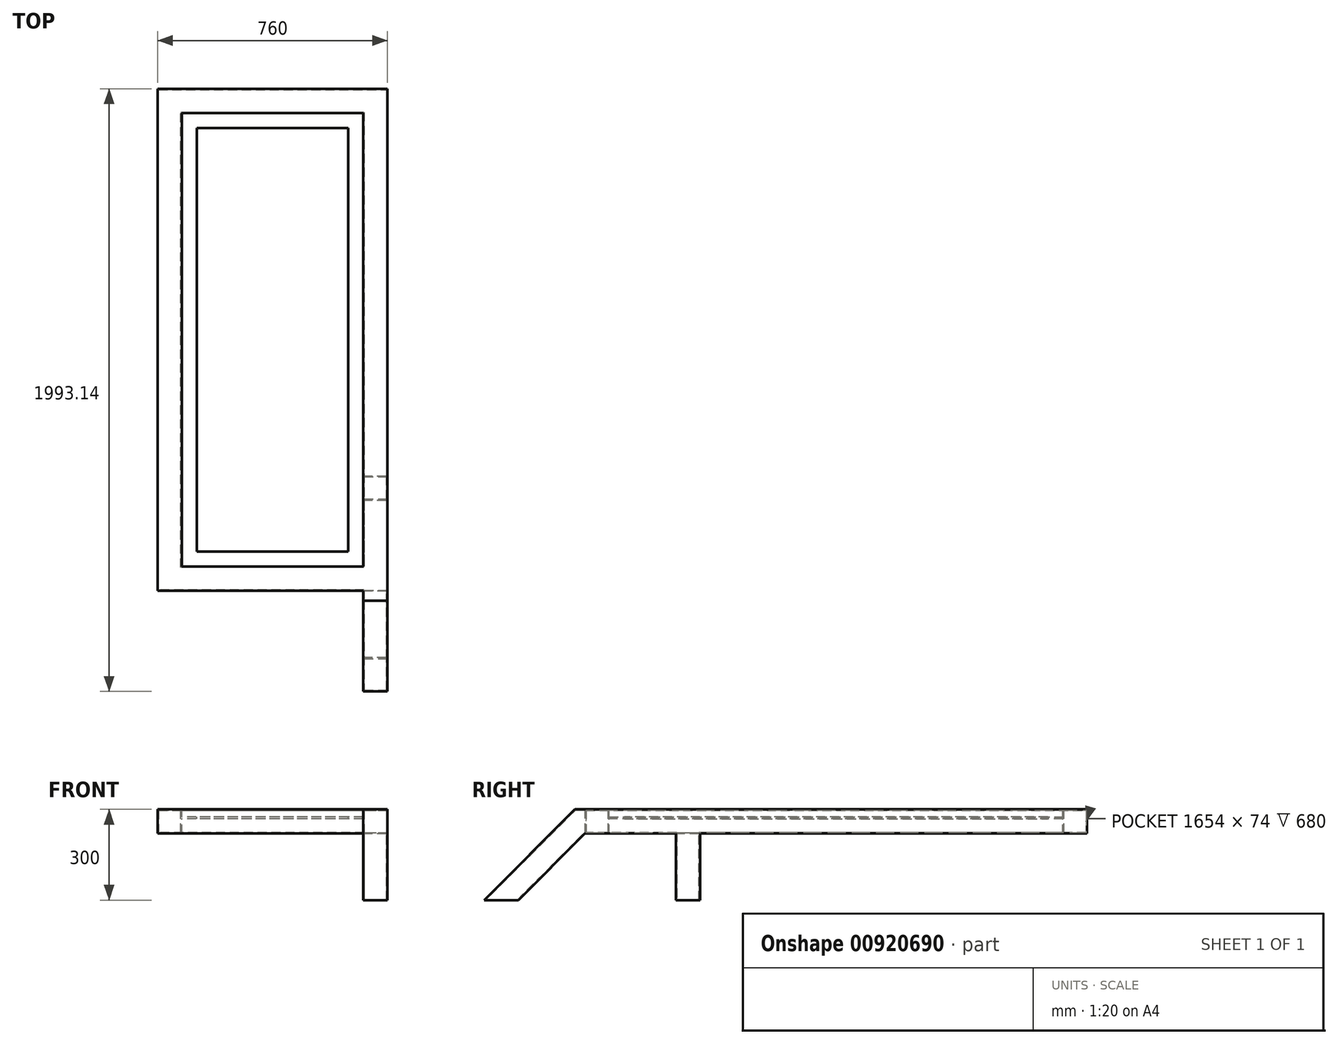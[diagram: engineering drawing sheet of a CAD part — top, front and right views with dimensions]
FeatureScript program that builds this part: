
annotation { "Feature Type Name" : "Feature", "Feature Type Description" : "" }
export const myFeature = defineFeature(function(context is Context, id is Id, definition is map)
    precondition{}
    {
        {
            var Q0;
            Q0=qCreatedBy(makeId("Top.planeOp"),FACE);
            var sketch = newSketch(context, id + "F0", { "sketchPlane" : qUnion([Q0])});
            skLineSegment(sketch, "E0.bottom", {"start": v(0, 0) * mm, "end": v(600, 0) * mm});
            skLineSegment(sketch, "E0.top", {"start": v(0, 1500) * mm, "end": v(600, 1500) * mm});
            skLineSegment(sketch, "E0.left", {"start": v(0, 0) * mm, "end": v(0, 1500) * mm});
            skLineSegment(sketch, "E0.right", {"start": v(600, 0) * mm, "end": v(600, 1500) * mm});
            skSolve(sketch);
        }
        {
            var Q0;
            Q0=qCreatedBy(makeId("Front.planeOp"),FACE);
            var sketch = newSketch(context, id + "F1", { "sketchPlane" : qUnion([Q0])});
            skLineSegment(sketch, "E1.bottom", {"start": v(0, -50) * mm, "end": v(-80, -50) * mm});
            skLineSegment(sketch, "E1.top", {"start": v(0, 30) * mm, "end": v(-80, 30) * mm});
            skLineSegment(sketch, "E1.left", {"start": v(0, -50) * mm, "end": v(0, -1) * mm});
            skLineSegment(sketch, "E1.right", {"start": v(-80, -50) * mm, "end": v(-80, 30) * mm});
            skLineSegment(sketch, "E2.bottom", {"start": v(0, 5) * mm, "end": v(50, 5) * mm});
            skLineSegment(sketch, "E2.top", {"start": v(0, -1) * mm, "end": v(50, -1) * mm});
            skLineSegment(sketch, "E2.right", {"start": v(50, 5) * mm, "end": v(50, -1) * mm});
            skLineSegment(sketch, "E3.trimOffspring", {"start": v(0, 5) * mm, "end": v(0, 30) * mm});
            skSolve(sketch);
        }
        {
            var Q0;
            Q0=makeQuery(id+"F1.imprint","IMPRINT",FACE,{"disambiguationData":[TD([[makeQuery(id+"F1.imprint","IMPRINT",EDGE,{"derivedFrom":sQuery(id+"F1.wireOp",EDGE,"E1.bottom")}),-1.0]])]});
            var Q1;
            Q1=sQuery(id+"F0.wireOp",EDGE,"E0.left");
            var Q2;
            Q2=sQuery(id+"F0.wireOp",EDGE,"E0.top");
            var Q3;
            Q3=sQuery(id+"F0.wireOp",EDGE,"E0.right");
            var Q4;
            Q4=sQuery(id+"F0.wireOp",EDGE,"E0.bottom");
            sweep(context, id + "F2", {"profiles" : qUnion([Q0]), "path" : qUnion([Q1, Q2, Q3, Q4])});
        }
        {
            var Q0;
            Q0=makeQuery(id+"F2.opSweep","SWEPT_FACE",FACE,{"disambiguationData":[OSD([sQuery(id+"F0.wireOp",EDGE,"E0.right"),sQuery(id+"F1.wireOp",EDGE,"E1.right")])]});
            var sketch = newSketch(context, id + "F3", { "sketchPlane" : qUnion([Q0])});
            skLineSegment(sketch, "E4", {"start": v(-80, 30) * mm, "end": v(-113.14, 30) * mm});
            skLineSegment(sketch, "E5", {"start": v(-113.14, 30) * mm, "end": v(-413.14, -270) * mm});
            skLineSegment(sketch, "E6", {"start": v(-413.14, -270) * mm, "end": v(-300, -270) * mm});
            skLineSegment(sketch, "E7", {"start": v(-300, -270) * mm, "end": v(-80, -50) * mm});
            skLineSegment(sketch, "E8", {"start": v(220, -50) * mm, "end": v(220, -270) * mm});
            skLineSegment(sketch, "E9", {"start": v(220, -270) * mm, "end": v(300, -270) * mm});
            skLineSegment(sketch, "E10", {"start": v(300, -270) * mm, "end": v(300, -50) * mm});
            skSolve(sketch);
        }
        {
            var Q0;
            Q0=makeQuery(id+"F3.imprint","IMPRINT",FACE,{"disambiguationData":[TD([[makeQuery(id+"F3.imprint","IMPRINT",EDGE,{"derivedFrom":sQuery(id+"F3.wireOp",EDGE,"E4")}),1.0]])]});
            var Q1;
            {var subQ0=sQuery(id+"F3.wireOp",EDGE,"E8");Q1=makeQuery(id+"F3.imprint","IMPRINT",FACE,{"disambiguationData":[TD([[makeQuery(id+"F3.imprint","IMPRINT",EDGE,{"derivedFrom":subQ0}),1.0]])]});}
            var Q2;
            {var subQ0=sQuery(id+"F3.wireOp",EDGE,"oBsIPKtL-zfQD-FOCN-7NP3-3SEpg1Q4HTcu");Q2=makeQuery(id+"F3.imprint","IMPRINT",FACE,{"disambiguationData":[TD([[makeQuery(id+"F3.imprint","IMPRINT",EDGE,{"derivedFrom":subQ0}),1.0]])]});}
            extrude(context, id + "F4", {"entities" : qUnion([Q0, Q1, Q2]), "operationType" : NewBodyOperationType.ADD, "oppositeDirection" : true, "depth" : 80 * mm, "offsetDistance" : 25 * mm});
        }
        {
            var Q0;
            {var subQ0=sQuery(id+"F1.wireOp",EDGE,"E1.right");Q0=makeQuery(id+"F4.boolean.opBoolean","MERGE",FACE,{"derivedFrom":[makeQuery(id+"F2.opSweep","SWEPT_FACE",FACE,{"disambiguationData":[OSD([sQuery(id+"F0.wireOp",EDGE,"E0.right"),subQ0])]}),makeQuery(id+"F4.opExtrude","CAP_FACE",FACE,{"disambiguationData":[OSD([sQuery(id+"F0.wireOp",VERTEX,"E0.bottom.end"),subQ0,sQuery(id+"F3.wireOp",EDGE,"E4"),sQuery(id+"F3.wireOp",EDGE,"E5"),sQuery(id+"F3.wireOp",EDGE,"E6"),sQuery(id+"F3.wireOp",EDGE,"E7")])],"isStart":true})]});}
            var Q1;
            Q1=makeQuery(id+"F2.opSweep","SWEPT_FACE",FACE,{"disambiguationData":[OSD([sQuery(id+"F0.wireOp",EDGE,"E0.left"),sQuery(id+"F1.wireOp",EDGE,"E1.right")])]});
            cPlane(context, id + "F5", {"entities" : qUnion([Q0, Q1]), "cplaneType" : CPlaneType.MID_PLANE, "offset" : 25 * mm, "width" : 150 * mm, "height" : 150 * mm});
        }
        {
            var Q0;
            Q0=makeQuery(id+"F2.opSweep","SWEPT_FACE",FACE,{"disambiguationData":[OSD([sQuery(id+"F0.wireOp",EDGE,"E0.bottom"),sQuery(id+"F1.wireOp",EDGE,"E1.right")])]});
            var Q1;
            Q1=makeQuery(id+"F2.opSweep","SWEPT_FACE",FACE,{"disambiguationData":[OSD([sQuery(id+"F0.wireOp",EDGE,"E0.top"),sQuery(id+"F1.wireOp",EDGE,"E1.right")])]});
            cPlane(context, id + "F6", {"entities" : qUnion([Q0, Q1]), "cplaneType" : CPlaneType.MID_PLANE, "offset" : 25 * mm, "width" : 150 * mm, "height" : 150 * mm});
        }
        {
            var Q0;
            Q0=makeQuery(id+"F6utSewFVofmKBA_1.1.F4.opExtrude","SWEPT_FACE",FACE,{"disambiguationData":[OSD([sQuery(id+"F3.wireOp",EDGE,"E6")])]});
            var Q1;
            Q1=makeQuery(id+"F6utSewFVofmKBA_1.1.F4.opExtrude","SWEPT_FACE",FACE,{"disambiguationData":[OSD([sQuery(id+"F3.wireOp",EDGE,"E9")])]});
            var Q2;
            Q2=makeQuery(id+"F4.opExtrude","SWEPT_FACE",FACE,{"disambiguationData":[OSD([sQuery(id+"F3.wireOp",EDGE,"E6")])]});
            var Q3;
            Q3=makeQuery(id+"F4.opExtrude","SWEPT_FACE",FACE,{"disambiguationData":[OSD([sQuery(id+"F3.wireOp",EDGE,"E9")])]});
            var Q4;
            Q4=makeQuery(id+"Fo37CPcSfJq6dBw_1.1.F4.opExtrude","SWEPT_FACE",FACE,{"disambiguationData":[OSD([sQuery(id+"F3.wireOp",EDGE,"E9")])]});
            var Q5;
            Q5=makeQuery(id+"Fo37CPcSfJq6dBw_1.1.F6utSewFVofmKBA_1.1.F4.opExtrude","SWEPT_FACE",FACE,{"disambiguationData":[OSD([sQuery(id+"F3.wireOp",EDGE,"E9")])]});
            var Q6;
            Q6=makeQuery(id+"Fo37CPcSfJq6dBw_1.1.F6utSewFVofmKBA_1.1.F4.opExtrude","SWEPT_FACE",FACE,{"disambiguationData":[OSD([sQuery(id+"F3.wireOp",EDGE,"E6")])]});
            var Q7;
            Q7=makeQuery(id+"Fo37CPcSfJq6dBw_1.1.F4.opExtrude","SWEPT_FACE",FACE,{"disambiguationData":[OSD([sQuery(id+"F3.wireOp",EDGE,"E6")])]});
            shell(context, id + "F7", {"entities" : qUnion([Q0, Q1, Q2, Q3, Q4, Q5, Q6, Q7]), "thickness" : 3 * mm});
        }
    });
